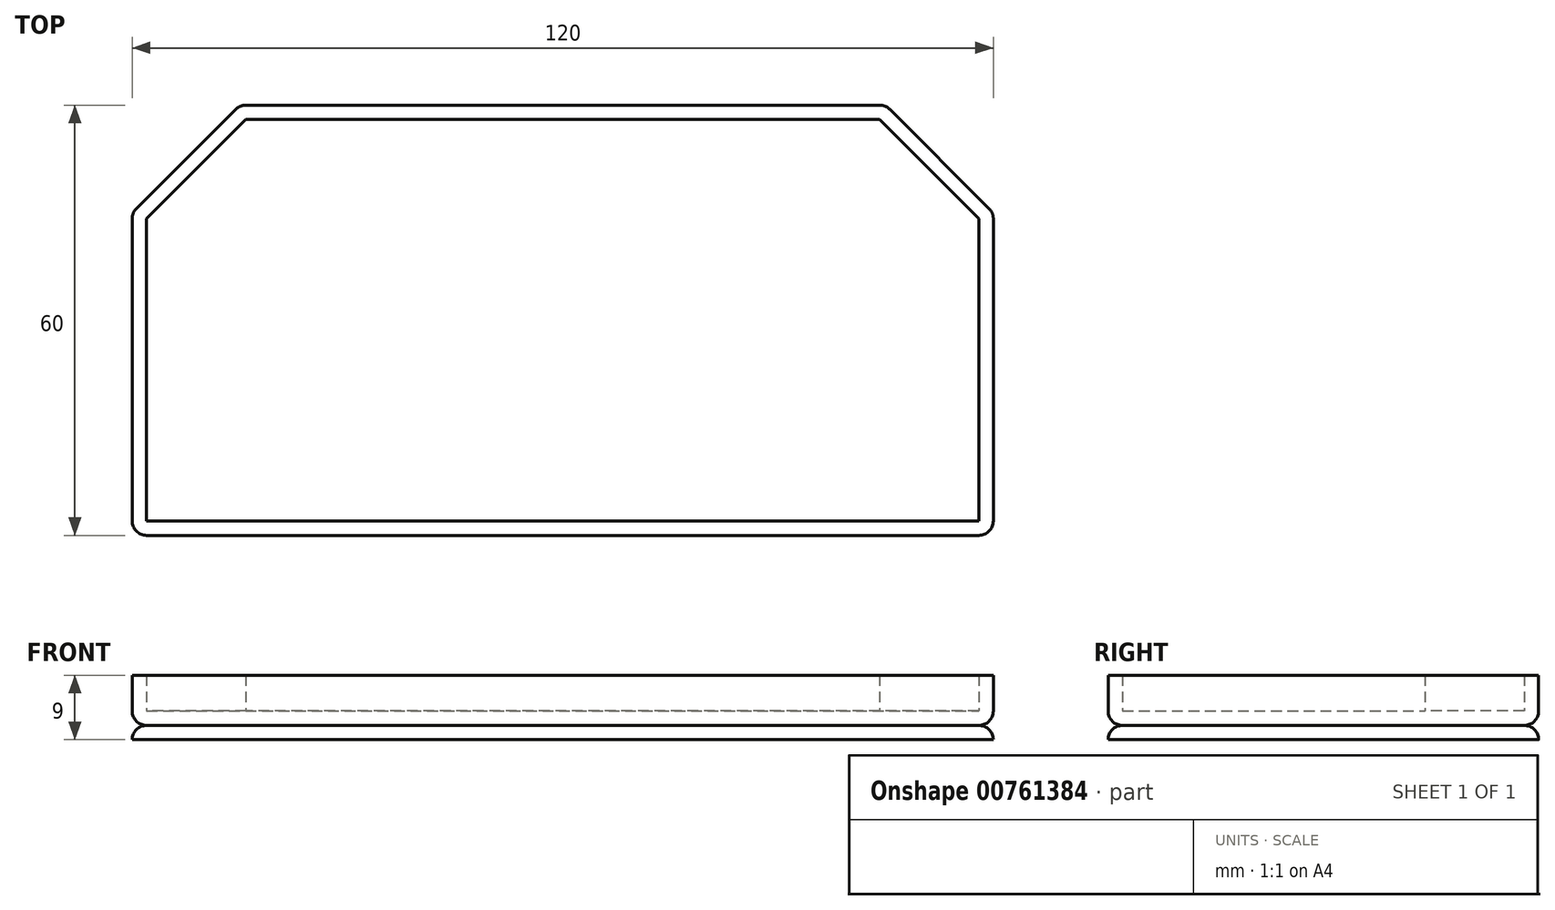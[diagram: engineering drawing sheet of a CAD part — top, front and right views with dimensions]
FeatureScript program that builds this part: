
annotation { "Feature Type Name" : "Feature", "Feature Type Description" : "" }
export const myFeature = defineFeature(function(context is Context, id is Id, definition is map)
    precondition{}
    {
        {
            var Q0;
            Q0=qCreatedBy(makeId("Top.planeOp"),FACE);
            var sketch = newSketch(context, id + "F0", { "sketchPlane" : qUnion([Q0])});
            skLineSegment(sketch, "E0", {"start": v(-58, -30) * mm, "end": v(58, -30) * mm});
            skLineSegment(sketch, "E1", {"start": v(60, -28) * mm, "end": v(60, 14.17) * mm});
            skLineSegment(sketch, "E2", {"start": v(59.41, 15.59) * mm, "end": v(45.59, 29.41) * mm});
            skLineSegment(sketch, "E3", {"start": v(44.17, 30) * mm, "end": v(-44.17, 30) * mm});
            skLineSegment(sketch, "E4", {"start": v(-45.59, 29.41) * mm, "end": v(-59.41, 15.59) * mm});
            skLineSegment(sketch, "E5", {"start": v(-60, 14.17) * mm, "end": v(-60, -28) * mm});
            skPoint(sketch, "E6.visualSharp", {"position": v(-60, 15) * mm});
            skArc(sketch, "E6.filletArc", {"start": v(-59.41, 15.59) * mm, "mid": v(-59.85, 14.94) * mm, "end": v(-60, 14.17) * mm});
            skPoint(sketch, "E7.visualSharp", {"position": v(-45, 30) * mm});
            skArc(sketch, "E7.filletArc", {"start": v(-44.17, 30) * mm, "mid": v(-44.94, 29.85) * mm, "end": v(-45.59, 29.41) * mm});
            skPoint(sketch, "E8.visualSharp", {"position": v(-60, -30) * mm});
            skArc(sketch, "E8.filletArc", {"start": v(-60, -28) * mm, "mid": v(-59.41, -29.41) * mm, "end": v(-58, -30) * mm});
            skPoint(sketch, "E9.visualSharp", {"position": v(60, -30) * mm});
            skArc(sketch, "E9.filletArc", {"start": v(58, -30) * mm, "mid": v(59.41, -29.41) * mm, "end": v(60, -28) * mm});
            skPoint(sketch, "E10.visualSharp", {"position": v(60, 15) * mm});
            skArc(sketch, "E10.filletArc", {"start": v(60, 14.17) * mm, "mid": v(59.85, 14.94) * mm, "end": v(59.41, 15.59) * mm});
            skPoint(sketch, "E11.visualSharp", {"position": v(45, 30) * mm});
            skArc(sketch, "E11.filletArc", {"start": v(45.59, 29.41) * mm, "mid": v(44.94, 29.85) * mm, "end": v(44.17, 30) * mm});
            skSolve(sketch);
        }
        {
            var Q0;
            Q0=makeQuery(id+"F0.imprint","IMPRINT",FACE,{"disambiguationData":[TD([[makeQuery(id+"F0.imprint","IMPRINT",EDGE,{"derivedFrom":sQuery(id+"F0.wireOp",EDGE,"E0")}),1.0]])]});
            extrude(context, id + "F1", {"entities" : qUnion([Q0]), "depth" : 2 * mm, "offsetDistance" : 25 * mm});
        }
        {
            var Q0;
            Q0=makeQuery(id+"F1.opExtrude","CAP_EDGE",EDGE,{"disambiguationData":[OSD([sQuery(id+"F0.wireOp",EDGE,"E0")])],"isStart":true});
            var Q1;
            Q1=makeQuery(id+"F1.opExtrude","CAP_EDGE",EDGE,{"disambiguationData":[OSD([sQuery(id+"F0.wireOp",EDGE,"E5")])],"isStart":true});
            var Q2;
            Q2=makeQuery(id+"F1.opExtrude","CAP_EDGE",EDGE,{"disambiguationData":[OSD([sQuery(id+"F0.wireOp",EDGE,"E3")])],"isStart":true});
            var Q3;
            Q3=makeQuery(id+"F1.opExtrude","CAP_EDGE",EDGE,{"disambiguationData":[OSD([sQuery(id+"F0.wireOp",EDGE,"E2")])],"isStart":true});
            var Q4;
            Q4=makeQuery(id+"F1.opExtrude","CAP_EDGE",EDGE,{"disambiguationData":[OSD([sQuery(id+"F0.wireOp",EDGE,"E1")])],"isStart":true});
            var Q5;
            Q5=makeQuery(id+"F1.opExtrude","CAP_EDGE",EDGE,{"disambiguationData":[OSD([sQuery(id+"F0.wireOp",EDGE,"E4")])],"isStart":true});
            fillet(context, id + "F2", {"entities" : qUnion([Q0, Q1, Q2, Q3, Q4, Q5]), "radius" : 2 * mm, "tangentPropagation" : true, "allowEdgeOverflow" : false});
        }
        {
            var Q0;
            Q0=makeQuery(id+"F1.opExtrude","CAP_FACE",FACE,{"disambiguationData":[OSD([sQuery(id+"F0.wireOp",EDGE,"E0"),sQuery(id+"F0.wireOp",EDGE,"E1"),sQuery(id+"F0.wireOp",EDGE,"E2"),sQuery(id+"F0.wireOp",EDGE,"E3"),sQuery(id+"F0.wireOp",EDGE,"E4"),sQuery(id+"F0.wireOp",EDGE,"E5"),sQuery(id+"F0.wireOp",EDGE,"E6.filletArc"),sQuery(id+"F0.wireOp",EDGE,"E7.filletArc"),sQuery(id+"F0.wireOp",EDGE,"E8.filletArc"),sQuery(id+"F0.wireOp",EDGE,"E9.filletArc"),sQuery(id+"F0.wireOp",EDGE,"E10.filletArc"),sQuery(id+"F0.wireOp",EDGE,"E11.filletArc")])],"isStart":false});
            var sketch = newSketch(context, id + "F3", { "sketchPlane" : qUnion([Q0])});
            skLineSegment(sketch, "E12.0", {"start": v(44.17, 28) * mm, "end": v(-44.17, 28) * mm});
            skLineSegment(sketch, "E12.1", {"start": v(-58, 14.17) * mm, "end": v(-58, -28) * mm});
            skLineSegment(sketch, "E12.2", {"start": v(-58, -28) * mm, "end": v(58, -28) * mm});
            skLineSegment(sketch, "E12.3", {"start": v(-44.17, 28) * mm, "end": v(-58, 14.17) * mm});
            skLineSegment(sketch, "E12.4", {"start": v(58, -28) * mm, "end": v(58, 14.17) * mm});
            skLineSegment(sketch, "E12.5", {"start": v(58, 14.17) * mm, "end": v(44.17, 28) * mm});
            skSolve(sketch);
        }
        {
            var Q0;
            Q0=makeQuery(id+"F3.imprint","IMPRINT",FACE,{"disambiguationData":[TD([[makeQuery(id+"F3.imprint","IMPRINT",EDGE,{"derivedFrom":sQuery(id+"F3.wireOp",EDGE,"E12.0")}),-1.0]])]});
            extrude(context, id + "F4", {"entities" : qUnion([Q0]), "operationType" : NewBodyOperationType.ADD, "depth" : 5 * mm, "offsetDistance" : 25 * mm});
        }
        {
            var Q0;
            Q0 = qSketchRegion(id + "F0", true);
            extrude(context, id + "F5", {"entities" : qUnion([Q0]), "oppositeDirection" : true, "depth" : 2 * mm, "offsetDistance" : 25 * mm});
        }
        {
            var Q0;
            Q0=makeQuery(id+"F5.opExtrude","CAP_EDGE",EDGE,{"disambiguationData":[OSD([sQuery(id+"F0.wireOp",EDGE,"E5")])],"isStart":true});
            fillet(context, id + "F6", {"entities" : qUnion([Q0]), "radius" : 2 * mm, "tangentPropagation" : true, "allowEdgeOverflow" : false});
        }
    });
